FCSTD DOCUMENT  (FreeCAD 0.15R4671 (Git))
Label: DDExtruderBody
License: All rights reserved
LicenseURL: http://en.wikipedia.org/wiki/All_rights_reserved
objects: Sketcher::SketchObject×10, PartDesign::Pocket×7, PartDesign::Fillet×7, Part::Feature×4, PartDesign::Pad×3, Mesh::Feature×2, PartDesign::Chamfer×2
note: 43 computed .brp shape members not serialized (recipe doc carries the construction recipe); baked Part::Feature solids carry a one-line shape summary decoded from their .brp

FEATURE [Part::Feature] Part__Feature  label="OB1515_180mm"
  Placement = pos=(-90,7.5,0) rot=(0,1,0;1.5708rad)
  shape: bbox 180 x 15 x 15 mm, 158 faces (baked)
FEATURE [Part::Feature] Part__Feature001  label="NEMA17"
  Placement = pos=(46,-0.5,-31) rot=(1,0,0;1.5708rad)
  shape: bbox 42.3 x 68 x 42.3 mm, 275 faces (baked)
FEATURE [Mesh::Feature] _08ZZ_Ball_Bearing  label="608ZZ_Ball_Bearing"
  Placement = pos=(28.5,-16,-31) rot=(1,0,0;1.5708rad)
FEATURE [Mesh::Feature] PNEUMATIC_NIPPLE
  Placement = pos=(46.8,-24.8,-2) rot=(0,-1,0;1.5708rad)
FEATURE [Sketcher::SketchObject] Sketch
  Placement = pos=(0,0,0) rot=(-1,0,0;4.71239rad)
  sketch-geometry (4):
    g0: LineSegment StartX=25 StartY=-52 StartZ=0 EndX=67 EndY=-52 EndZ=0
    g1: LineSegment StartX=67 StartY=-52 StartZ=0 EndX=67 EndY=7.37741 EndZ=0
    g2: LineSegment StartX=67 StartY=7.37741 StartZ=0 EndX=25 EndY=7.37741 EndZ=0
    g3: LineSegment StartX=25 StartY=7.37741 StartZ=0 EndX=25 EndY=-52 EndZ=0
  constraints (8):
    c: Coincident(g0,g1)
    c: Coincident(g1,g2)
    c: Coincident(g2,g3)
    c: Coincident(g3,g0)
    c: Horizontal(g0)
    c: Horizontal(g2)
    c: Vertical(g1)
    c: Vertical(g3)
FEATURE [PartDesign::Pad] Pad
  Length = 7
  Length2 = 100
  Placement = pos=(0,0,0) rot=(-1,0,0;4.71239rad)
  Sketch = -> Sketch
  Type = 0
FEATURE [Sketcher::SketchObject] Sketch001
  Placement = pos=(0,-7,0) rot=(1,0,0;1.5708rad)
  Support = -> Pad [Face6]
  sketch-geometry (1):
    g0: Circle CenterX=46 CenterY=-31 CenterZ=0 NormalX=0 NormalY=0 NormalZ=1 Radius=12
  constraints (1):
    c: Radius(g0) = 12
FEATURE [PartDesign::Pocket] Pocket
  Length = 5
  Placement = pos=(0,0,0) rot=(-1,0,0;4.71239rad)
  Sketch = -> Sketch001
  Type = 1
FEATURE [Part::Feature] Part__Feature002  label="Mk7_DriveGear"
  Placement = pos=(46,-9,-31) rot=(1,0,0;1.5708rad)
  shape: bbox 15.07 x 10 x 15.07 mm, 6 faces (baked)
FEATURE [Sketcher::SketchObject] Sketch002
  Placement = pos=(0,-7,0) rot=(1,0,0;1.5708rad)
  Support = -> Pocket [Face5]
  sketch-geometry (4):
    g0: LineSegment StartX=25 StartY=7.37838 StartZ=0 EndX=52.4457 EndY=7.37838 EndZ=0
    g1: LineSegment StartX=52.4457 StartY=7.37838 StartZ=0 EndX=52.4457 EndY=-31.0411 EndZ=0
    g2: LineSegment StartX=52.4457 StartY=-31.0411 StartZ=0 EndX=25 EndY=-31.0411 EndZ=0
    g3: LineSegment StartX=25 StartY=-31.0411 StartZ=0 EndX=25 EndY=7.37838 EndZ=0
  constraints (8):
    c: Coincident(g0,g1)
    c: Coincident(g1,g2)
    c: Coincident(g2,g3)
    c: Coincident(g3,g0)
    c: Horizontal(g0)
    c: Horizontal(g2)
    c: Vertical(g1)
    c: Vertical(g3)
FEATURE [PartDesign::Pad] Pad001
  Length = 20
  Length2 = 100
  Placement = pos=(0,0,0) rot=(-1,0,0;4.71239rad)
  Sketch = -> Sketch002
  Type = 0
FEATURE [Sketcher::SketchObject] Sketch003
  Placement = pos=(0,-27,0) rot=(1,0,0;1.5708rad)
  Support = -> Pad001 [Face10]
  sketch-geometry (1):
    g0: Circle CenterX=46 CenterY=-31 CenterZ=0 NormalX=0 NormalY=0 NormalZ=1 Radius=7
  constraints (1):
    c: Radius(g0) = 7
FEATURE [PartDesign::Pocket] Pocket001
  Length = 5
  Placement = pos=(0,0,0) rot=(-1,0,0;4.71239rad)
  Sketch = -> Sketch003
  Type = 1
FEATURE [Sketcher::SketchObject] Sketch004
  Placement = pos=(0,0,7.37838) rot=(0,0,1;3.14159rad)
  Support = -> Pocket001 [Face9]
  sketch-geometry (1):
    g0: Circle CenterX=-40 CenterY=16 CenterZ=0 NormalX=0 NormalY=0 NormalZ=1 Radius=1
  constraints (1):
    c: Radius(g0) = 1
FEATURE [PartDesign::Pocket] Pocket002
  Length = 5
  Placement = pos=(0,0,0) rot=(-1,0,0;4.71239rad)
  Sketch = -> Sketch004
  Type = 1
FEATURE [Sketcher::SketchObject] Sketch005
  Placement = pos=(0,-7,0) rot=(1,0,0;1.5708rad)
  Support = -> Pocket002 [Face5]
  sketch-geometry (4):
    g0: LineSegment StartX=37 StartY=-43.5 StartZ=0 EndX=43 EndY=-43.5 EndZ=0
    g1: LineSegment StartX=43 StartY=-43.5 StartZ=0 EndX=43 EndY=-52 EndZ=0
    g2: LineSegment StartX=43 StartY=-52 StartZ=0 EndX=37 EndY=-52 EndZ=0
    g3: LineSegment StartX=37 StartY=-52 StartZ=0 EndX=37 EndY=-43.5 EndZ=0
  constraints (8):
    c: Coincident(g0,g1)
    c: Coincident(g1,g2)
    c: Coincident(g2,g3)
    c: Coincident(g3,g0)
    c: Horizontal(g0)
    c: Horizontal(g2)
    c: Vertical(g1)
    c: Vertical(g3)
FEATURE [PartDesign::Pad] Pad002
  Length = 12.5
  Length2 = 100
  Placement = pos=(0,0,0) rot=(-1,0,0;4.71239rad)
  Sketch = -> Sketch005
  Type = 0
FEATURE [Sketcher::SketchObject] Sketch006
  Placement = pos=(0,0,-52) rot=(1,0,0;3.14159rad)
  Support = -> Pad002 [Face20]
  sketch-geometry (1):
    g0: Circle CenterX=40 CenterY=16 CenterZ=0 NormalX=0 NormalY=0 NormalZ=1 Radius=1
  constraints (1):
    c: Radius(g0) = 1
FEATURE [PartDesign::Pocket] Pocket003
  Length = 15
  Placement = pos=(0,0,0) rot=(-1,0,0;4.71239rad)
  Sketch = -> Sketch006
  Type = 0
FEATURE [PartDesign::Fillet] Fillet
  Base = -> Pocket003 [Edge22]
  Placement = pos=(0,0,0) rot=(-1,0,0;4.71239rad)
  Radius = 1.9
FEATURE [PartDesign::Fillet] Fillet001
  Base = -> Fillet [Edge32,Edge35]
  Placement = pos=(0,0,0) rot=(-1,0,0;4.71239rad)
  Radius = 2.99
FEATURE [PartDesign::Fillet] Fillet002
  Base = -> Fillet001 [Edge13,Edge18]
  Placement = pos=(0,0,0) rot=(-1,0,0;4.71239rad)
  Radius = 9
FEATURE [PartDesign::Chamfer] Chamfer
  Base = -> Fillet002 [Edge6,Edge10]
  Placement = pos=(0,0,0) rot=(-1,0,0;4.71239rad)
  Size = 4
FEATURE [Part::Feature] Chamfer001
  shape: bbox 42 x 27 x 59.38 mm, 28 faces (baked)
FEATURE [Sketcher::SketchObject] Sketch007
  Placement = pos=(0,0,7.37838) rot=(0,0,1;0rad)
  Support = -> Chamfer001 [Face23]
  sketch-geometry (1):
    g0: Circle CenterX=40 CenterY=-16 CenterZ=0 NormalX=0 NormalY=0 NormalZ=1 Radius=4.75
  constraints (1):
    c: Radius(g0) = 4.75
FEATURE [PartDesign::Pocket] Pocket004
  Length = 6
  Sketch = -> Sketch007
  Type = 0
FEATURE [PartDesign::Chamfer] Chamfer002
  Base = -> Pocket004 [Edge84]
  Size = 3
FEATURE [Sketcher::SketchObject] Sketch008
  Placement = pos=(0,-27,0) rot=(1,0,0;1.5708rad)
  Support = -> Chamfer002 [Face5]
  sketch-geometry (7):
    g0: LineSegment StartX=44 StartY=-24.5 StartZ=0 EndX=44 EndY=-9.5 EndZ=0
    g1: LineSegment StartX=44 StartY=-9.5 StartZ=0 EndX=47.5 EndY=-9.5 EndZ=0
    g2: LineSegment StartX=47.5 StartY=-9.5 StartZ=0 EndX=47.5 EndY=8 EndZ=0
    g3: LineSegment StartX=47.5 StartY=8 StartZ=0 EndX=54.5 EndY=8 EndZ=0
    g4: LineSegment StartX=54.5 StartY=8 StartZ=0 EndX=54.5 EndY=-30.5 EndZ=0
    g5: LineSegment StartX=54.5 StartY=-30.5 StartZ=0 EndX=46.5 EndY=-30.5 EndZ=0
    g6: LineSegment StartX=46.5 StartY=-30.5 StartZ=0 EndX=44 EndY=-24.5 EndZ=0
  constraints (12):
    c: Vertical(g0)
    c: Coincident(g0,g1)
    c: Coincident(g1,g2)
    c: Vertical(g2)
    c: Coincident(g2,g3)
    c: Horizontal(g3)
    c: Coincident(g3,g4)
    c: Vertical(g4)
    c: Coincident(g4,g5)
    c: Horizontal(g5)
    c: Coincident(g5,g6)
    c: Coincident(g6,g0)
FEATURE [PartDesign::Pocket] Pocket005
  Length = 20
  Sketch = -> Sketch008
  Type = 0
FEATURE [Sketcher::SketchObject] Sketch009
  Placement = pos=(25,0,0) rot=(0.57735,-0.57735,-0.57735;2.0944rad)
  Support = -> Pocket005 [Face14]
  sketch-geometry (7):
    g0: LineSegment StartX=19 StartY=-42.5 StartZ=0 EndX=19 EndY=-23 EndZ=0
    g1: LineSegment StartX=19 StartY=-23 StartZ=0 EndX=19 EndY=-9.5 EndZ=0
    g2: LineSegment StartX=19 StartY=-9.5 StartZ=0 EndX=24.5 EndY=-9.5 EndZ=0
    g3: LineSegment StartX=24.5 StartY=-9.5 StartZ=0 EndX=24.5 EndY=8.30508 EndZ=0
    g4: LineSegment StartX=24.5 StartY=8.30508 StartZ=0 EndX=28.5 EndY=8.30508 EndZ=0
    g5: LineSegment StartX=28.5 StartY=8.30508 StartZ=0 EndX=28.5 EndY=-42.5 EndZ=0
    g6: LineSegment StartX=28.5 StartY=-42.5 StartZ=0 EndX=19 EndY=-42.5 EndZ=0
  constraints (14):
    c: Vertical(g0)
    c: Vertical(g1)
    c: Coincident(g1,g2)
    c: Coincident(g2,g3)
    c: Vertical(g3)
    c: Coincident(g3,g4)
    c: Coincident(g4,g5)
    c: Vertical(g5)
    c: Coincident(g5,g6)
    c: PointOnObject(g6,g0)
    c: Horizontal(g6)
    c: Coincident(g0,g6)
    c: Horizontal(g4)
    c: Coincident(g0,g1)
FEATURE [PartDesign::Pocket] Pocket006
  Length = 5
  Sketch = -> Sketch009
  Type = 1
FEATURE [PartDesign::Fillet] Fillet003
  Base = -> Pocket006 [Edge62]
  Radius = 6
FEATURE [PartDesign::Fillet] Fillet004
  Base = -> Fillet003 [Edge57]
  Radius = 4
FEATURE [PartDesign::Fillet] Fillet005
  Base = -> Fillet004 [Edge7,Edge2]
  Radius = 1.6
FEATURE [PartDesign::Fillet] Fillet006
  Base = -> Fillet005 [Edge55]
  Radius = 4
